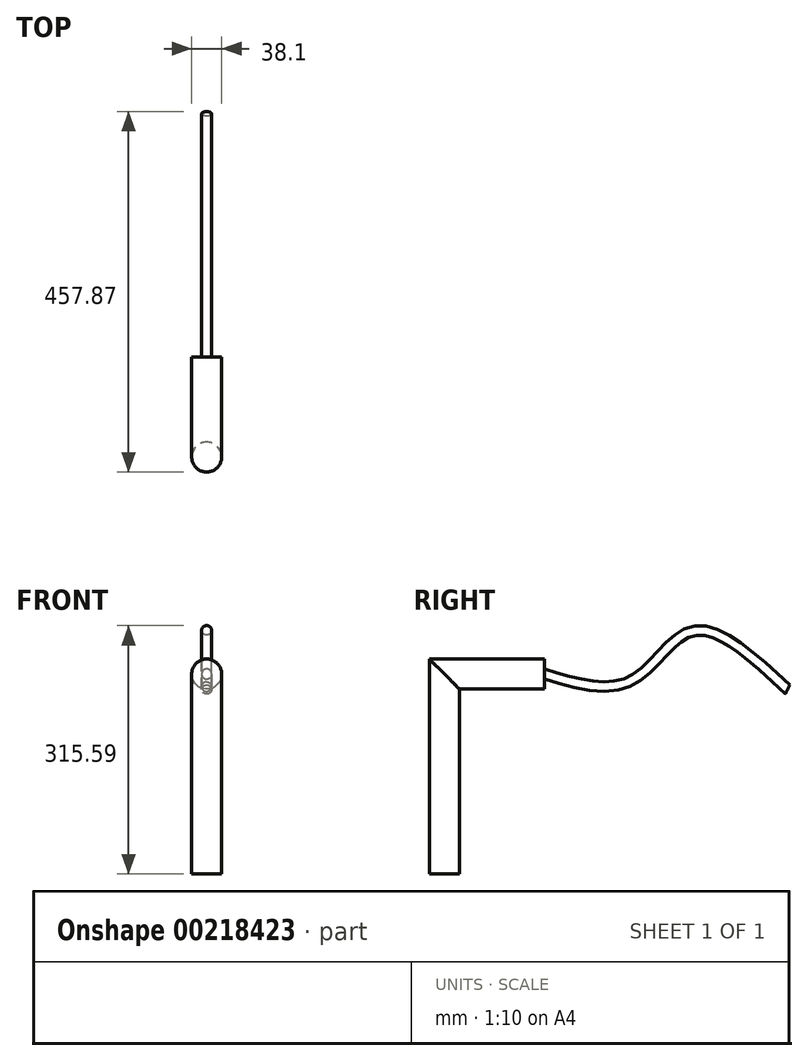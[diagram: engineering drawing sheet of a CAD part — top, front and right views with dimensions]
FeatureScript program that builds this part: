
annotation { "Feature Type Name" : "Feature", "Feature Type Description" : "" }
export const myFeature = defineFeature(function(context is Context, id is Id, definition is map)
    precondition{}
    {
        {
            var Q0;
            Q0=qCreatedBy(makeId("Right.planeOp"),FACE);
            var sketch = newSketch(context, id + "F0", { "sketchPlane" : qUnion([Q0])});
            skLineSegment(sketch, "E0", {"start": v(127, 0) * mm, "end": v(0, 0) * mm});
            skLineSegment(sketch, "E1", {"start": v(0, 0) * mm, "end": v(0, -254) * mm});
            skSolve(sketch);
        }
        {
            var Q0;
            Q0=qCreatedBy(makeId("Top.planeOp"),FACE);
            cPlane(context, id + "F1", {"entities" : qUnion([Q0]), "cplaneType" : CPlaneType.OFFSET, "offset" : 254 * mm, "oppositeDirection" : true, "width" : 152.4 * mm, "height" : 152.4 * mm});
        }
        {
            var Q0;
            Q0=qCreatedBy(id+"F1.planeOp",FACE);
            var sketch = newSketch(context, id + "F2", { "sketchPlane" : qUnion([Q0])});
            skCircle(sketch, "E2", {"center": v(0, 0) * mm, "radius": 19.05 * mm});
            skSolve(sketch);
        }
        {
            var Q0;
            Q0=makeQuery(id+"F2.imprint","IMPRINT",FACE,{"disambiguationData":[TD([[makeQuery(id+"F2.imprint","IMPRINT",EDGE,{"derivedFrom":sQuery(id+"F2.wireOp",EDGE,"E2")}),1.0]])]});
            var Q1;
            Q1=sQuery(id+"F0.wireOp",EDGE,"E1");
            var Q2;
            Q2=sQuery(id+"F0.wireOp",EDGE,"E0");
            sweep(context, id + "F3", {"profiles" : qUnion([Q0]), "path" : qUnion([Q1, Q2])});
        }
        {
            var Q0;
            Q0=qCreatedBy(makeId("Right.planeOp"),FACE);
            var sketch = newSketch(context, id + "F4", { "sketchPlane" : qUnion([Q0])});
            skFitSpline(sketch, "E3", {"points": [v(127, 0) * mm, v(237.86, -8.18) * mm, v(315.28, 54.52) * mm, v(436.02, -19.65) * mm], "startDerivative": vector(370.1, -112.56) * mm, "endDerivative": vector(357.46, -334.94) * mm});
            skSolve(sketch);
        }
        {
            var Q0;
            Q0=makeQuery(id+"F3.opSweep","CAP_FACE",FACE,{"disambiguationData":[OSD([sQuery(id+"F0.wireOp",VERTEX,"E0.start"),sQuery(id+"F2.wireOp",EDGE,"E2")])],"isStart":false});
            var sketch = newSketch(context, id + "F5", { "sketchPlane" : qUnion([Q0])});
            skCircle(sketch, "E4", {"center": v(0, 0) * mm, "radius": 6.35 * mm});
            skSolve(sketch);
        }
        {
            var Q0;
            Q0=makeQuery(id+"F5.imprint","IMPRINT",FACE,{"disambiguationData":[TD([[makeQuery(id+"F5.imprint","IMPRINT",EDGE,{"derivedFrom":sQuery(id+"F5.wireOp",EDGE,"E4")}),1.0]])]});
            var Q1;
            Q1=sQuery(id+"F4.wireOp",EDGE,"E3");
            sweep(context, id + "F6", {"operationType" : NewBodyOperationType.ADD, "profiles" : qUnion([Q0]), "path" : qUnion([Q1])});
        }
    });
